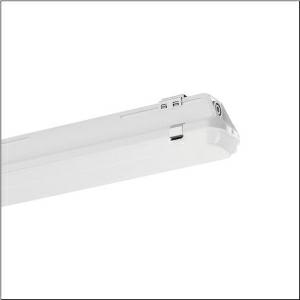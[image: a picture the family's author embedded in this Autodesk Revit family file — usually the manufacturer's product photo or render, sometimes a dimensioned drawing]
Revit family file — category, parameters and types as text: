
# Revit family: monsun_r__21_51fb10dp660b_51d9
name_source: partatom
category: Lighting Fixtures
units: mm (PartAtom-declared; Revit-internal decimal feet)

## family parameters
Cut with Voids When Loaded = No
Host = Face
Light Source = No
Part Type = Normal
Room Calculation Point = No
Round Connector Dimension = Use Diameter
Shared = No

## types (1)
- --- (1 x LED, 6060 lm, 39.4 W, 6500K)
    Apparent Load = 39 VA
    CIE Flux Codes = 47 77 93 94 100
    Color Rendering = 80
    Color Temperature = 6500K
    Default Elevation = 1800 mm
    Description = Monsun® 21, damp-proof luminaire, chain hanger, primary optical cover: enclosure, of PMMA, light emission: direct distribution, primary light characteristic: symmetric, installation type: suspended mounting, surface-mounted, horizontal mounting, vertical mounting, LED, rated luminous flux: 6.060lm, luminous efficacy: 154lm/W, light colour: 865, colour temperature: 6500K, control gear: DALI 2, with terminal, 5-pole, max. 2.5mm², mains connection: 220..240V, AC, 50/60Hz, rated input power: 39W, housing, of glass-fibre reinforced polyester, uncoated, bright grey, incl. chain hanger, length: 1.590mm, width: 90mm, height: 88mm, clip for enclosure, of stainless steel (V2A), ceiling mounting element, of stainless steel (V2A), chain hanger, of stainless steel (V2A), protection rating (complete): IP66, insulation class (complete): insulation class I (protective earthing), certification: CE, ENEC, VDE, UKCA, protection symbol: D, impact resistance: IK04, permissible operating ambient temperature: -25..+35°C, standard: EN 50419, EN 60598-2-1, corresponds to IFS (International Featured Standards) requirements for safety and quality in the food industry, for indoor or canopied outdoor use, no direct snow, no direct sun, no direct rain, contact your sales advisor before using the luminaires in applications with unclear chemical exposure, large temperature fluctuations or condensation-forming humidity, LABS conformity tested according to VDMA 24364:2018-05, packaging unit: 1 piece
    Height = 89 mm
    Lamp = 1 x LED
    Lamp Light Flux = 6060 lm
    Lamp Power = 39.4 W
    Lamp count = 1
    Length = 1590 mm
    Luminous efficacy = 154 lm/W
    Manufacturer = Siteco
    ModVariant = No
    Model = 51FB10DP660B
    Mounting Place = Ceiling
    Mounting Type = Surface mounted
    Number of Poles = 1
    OnlyDefault = Yes
    Power Factor = 1
    Product Name = Monsun® 21
    Product group = damp-proof luminaire
    ProductGroupID = 300
    Protection Class = Protection class I
    Protection Degree = IP 66
    RLX_Detail_Level = 1
    RLX_Emergency_Light_Flux = 0 lm
    RLX_Emergency_Type = 0
    RLX_Emergency_Type_DB = No
    RlxData = <blob elided: 92277 chars, md5=79267548>
    Socket = socket
    Standby Power = 0 W
    System Light Flux = 6060 lm
    System Power = 39 W
    Type Comments = factory setting: luminous flux: 100 % | dim-lin: 254 | 261 mA
    Type Image = l_1319656.jpg
    URL = http://relux.com
    VarID = @adj_197300
    Voltage = 0 V
    Weight = 0.00 kg
    Width = 90 mm

## geometry (parser evidence)
native form markers: Blend x4, Sweep x14
no freeform markers — native parametric forms only
